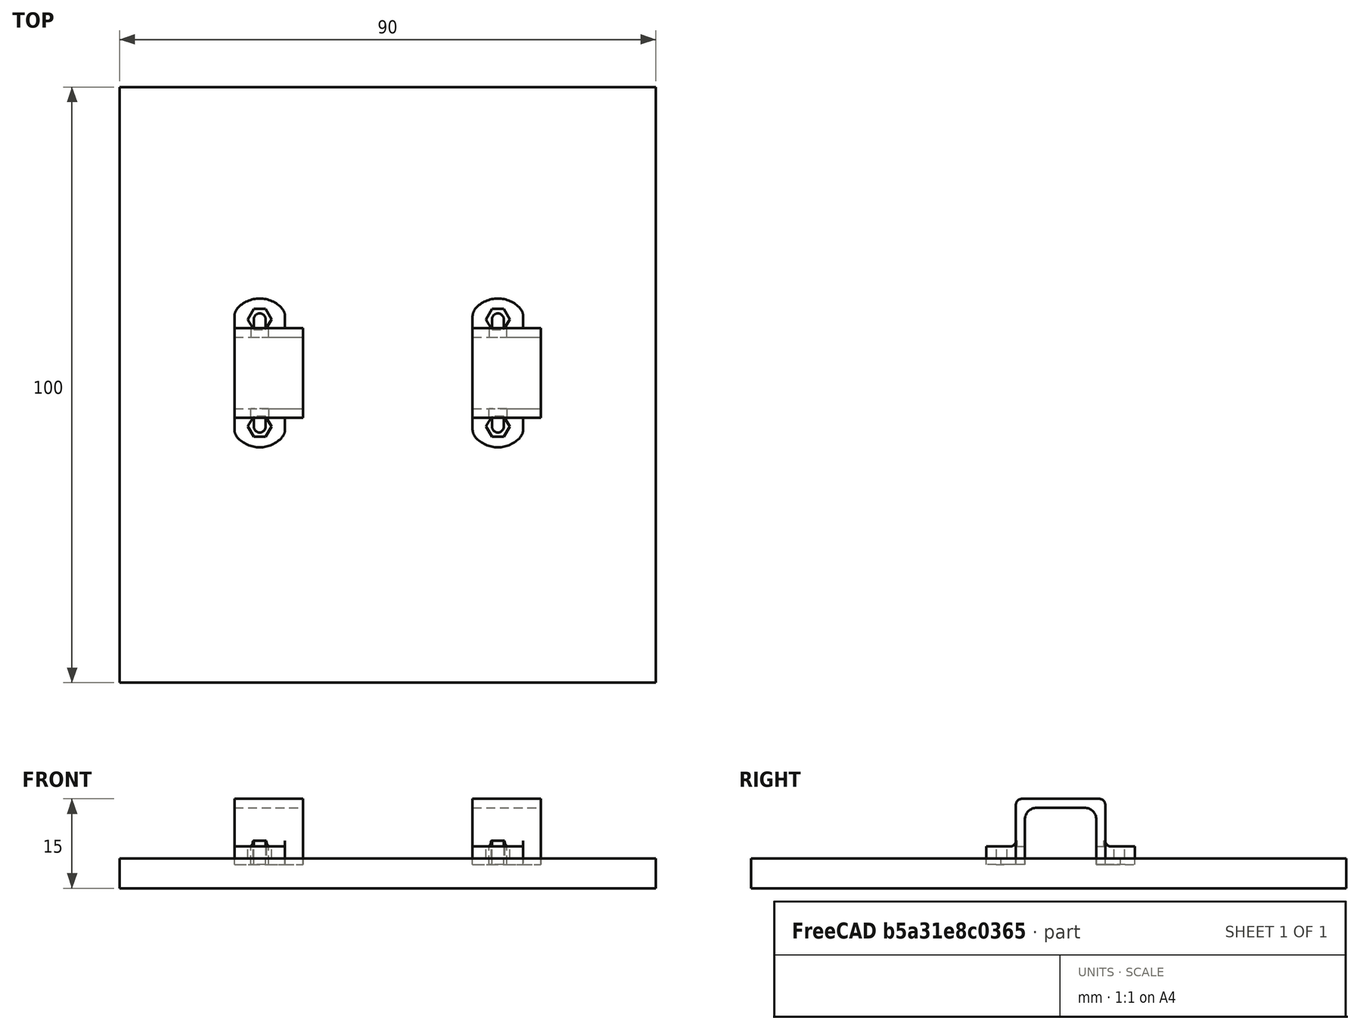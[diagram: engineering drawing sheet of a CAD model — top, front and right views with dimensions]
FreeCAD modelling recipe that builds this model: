
FCSTD DOCUMENT  (FreeCAD 1.0R39285 (Git))
Label: micromouse_assembly
License: All rights reserved
LicenseURL: https://en.wikipedia.org/wiki/All_rights_reserved
objects: Mesh::Feature×2, Part::Feature×2, Sketcher::SketchObject×1, PartDesign::Pad×1, PartDesign::Body×1
note: 8 computed .brp shape members not serialized (recipe doc carries the construction recipe); baked Part::Feature solids carry a one-line shape summary decoded from their .brp

FEATURE [Sketcher::SketchObject] Sketch
  ArcFitTolerance = 1e-06
  AttachmentSupport = -> [XY_Plane]
  FullyConstrained = true
  MakeInternals = false
  MapMode = 5
  sketch-geometry (4):
    g0: LineSegment StartX=-45 StartY=50 StartZ=0 EndX=-45 EndY=-50 EndZ=0
    g1: LineSegment StartX=-45 StartY=-50 StartZ=0 EndX=45 EndY=-50 EndZ=0
    g2: LineSegment StartX=45 StartY=-50 StartZ=0 EndX=45 EndY=50 EndZ=0
    g3: LineSegment StartX=45 StartY=50 StartZ=0 EndX=-45 EndY=50 EndZ=0
  constraints (12):
    c: Coincident(g0,g1)
    c: Coincident(g1,g2)
    c: Coincident(g2,g3)
    c: Coincident(g3,g0)
    c: Vertical(g0)
    c: Vertical(g2)
    c: Horizontal(g1)
    c: Horizontal(g3)
    c: DistanceX(g3,g3) = 90
    c: DistanceY(g0,g0) = 100
    c: Distance(g-2,g2) = 45
    c: Distance(g1,g-1) = 50
FEATURE [PartDesign::Pad] Pad
  Direction = (0,0,1)
  Length = 5
  Length2 = 10
  Profile = -> Sketch [Edge3,Edge4,Edge1,Edge2]
  ReferenceAxis = -> Sketch [N_Axis]
  Refine = true
  Suppressed = false
  Type = 0
FEATURE [PartDesign::Body] Body
  AllowCompound = false
  Group = -> [Sketch,Pad]
  Origin = -> Origin
  Tip = -> Pad
FEATURE [Mesh::Feature] n20ENCODED
  Placement = pos=(-100,233,3) rot=(0,0,1;3.14159rad)
FEATURE [Mesh::Feature] n20ENCODED001
  Placement = pos=(100,-230,3) rot=(0,0,1;0rad)
FEATURE [Part::Feature] Part__Feature  label="N20 support v7"
  Placement = pos=(20,2,4) rot=(0,0,1;4.71239rad)
  shape: bbox 11.5 x 25 x 11 mm, 60 faces (baked)
FEATURE [Part::Feature] Part__Feature001  label="N20 support v008"
  Placement = pos=(-20,2,4) rot=(0,0,1;4.71239rad)
  shape: bbox 11.5 x 25 x 11 mm, 60 faces (baked)
